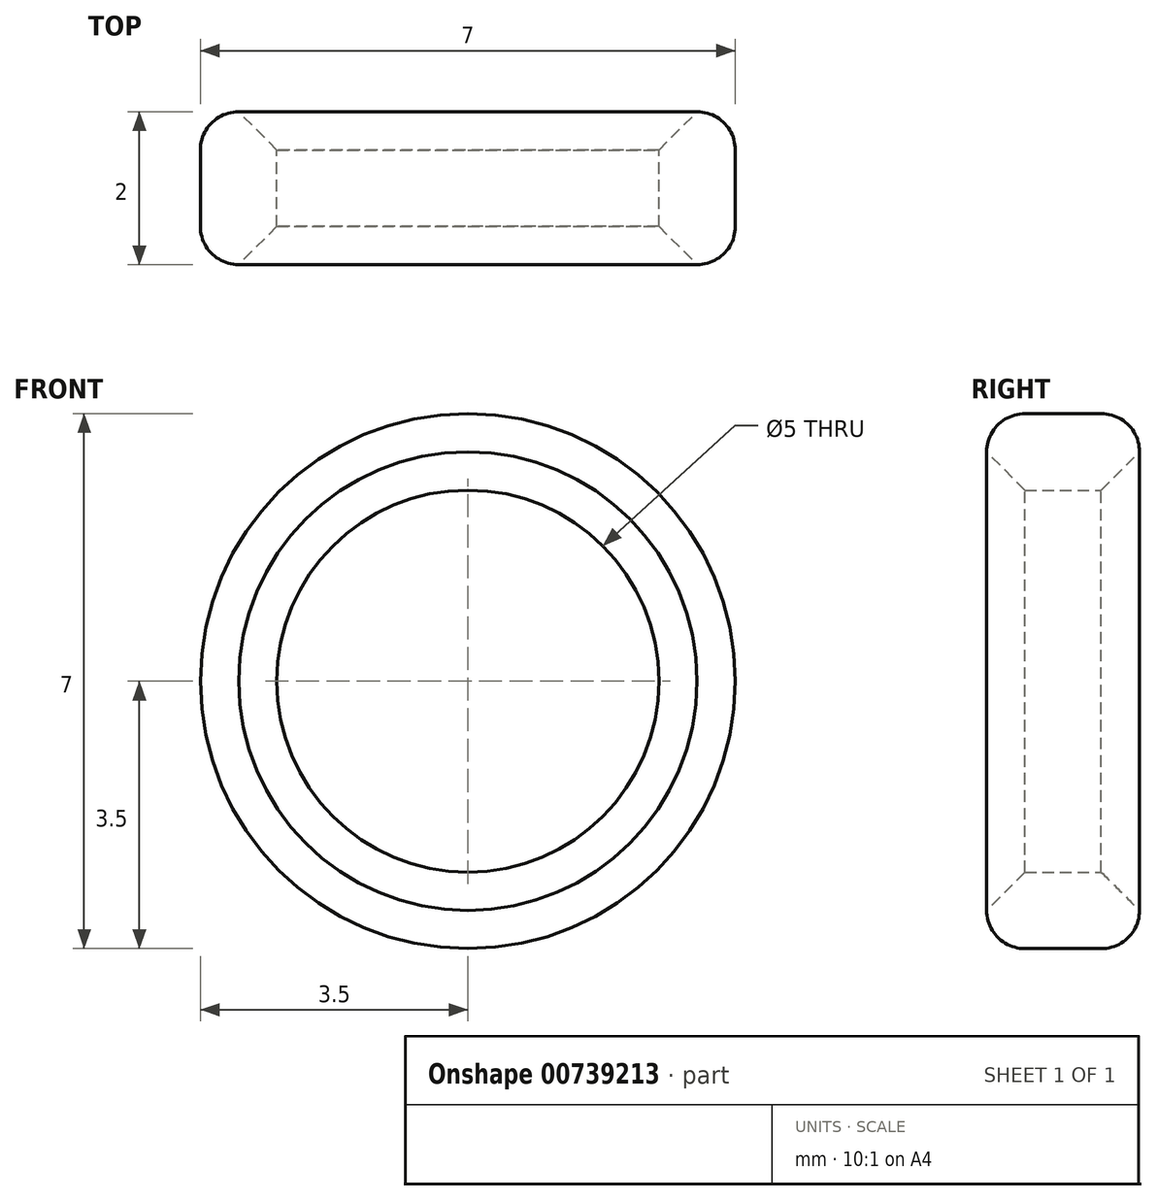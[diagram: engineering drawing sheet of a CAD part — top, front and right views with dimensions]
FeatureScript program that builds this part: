
annotation { "Feature Type Name" : "Feature", "Feature Type Description" : "" }
export const myFeature = defineFeature(function(context is Context, id is Id, definition is map)
    precondition{}
    {
        {
            var Q0;
            Q0=qCreatedBy(makeId("Front.planeOp"),FACE);
            var sketch = newSketch(context, id + "F0", { "sketchPlane" : qUnion([Q0])});
            skCircle(sketch, "E0", {"center": v(0, 0) * mm, "radius": 3.5 * mm});
            skCircle(sketch, "E1", {"center": v(0, 0) * mm, "radius": 2.5 * mm});
            skSolve(sketch);
        }
        {
            var Q0;
            Q0 = qSketchRegion(id + "F0", true);
            extrude(context, id + "F1", {"entities" : qUnion([Q0]), "depth" : 2 * mm, "offsetDistance" : 25.4 * mm});
        }
        {
            var Q0;
            Q0=makeQuery(id+"F1.opExtrude","CAP_EDGE",EDGE,{"disambiguationData":[OSD([sQuery(id+"F0.wireOp",EDGE,"E0")])],"isStart":false});
            var Q1;
            Q1=makeQuery(id+"F1.opExtrude","SWEPT_FACE",FACE,{"disambiguationData":[OSD([sQuery(id+"F0.wireOp",EDGE,"E0")])]});
            fillet(context, id + "F2", {"entities" : qUnion([Q0, Q1]), "radius" : 0.5 * mm, "tangentPropagation" : true, "allowEdgeOverflow" : false});
        }
        {
            var Q0;
            Q0=makeQuery(id+"F1.opExtrude","CAP_EDGE",EDGE,{"disambiguationData":[OSD([sQuery(id+"F0.wireOp",EDGE,"E1")])],"isStart":false});
            var Q1;
            Q1=makeQuery(id+"F1.opExtrude","CAP_EDGE",EDGE,{"disambiguationData":[OSD([sQuery(id+"F0.wireOp",EDGE,"E1")])],"isStart":true});
            chamfer(context, id + "F3", {"entities" : qUnion([Q0, Q1]), "width" : 0.5 * mm, "tangentPropagation" : true});
        }
    });
